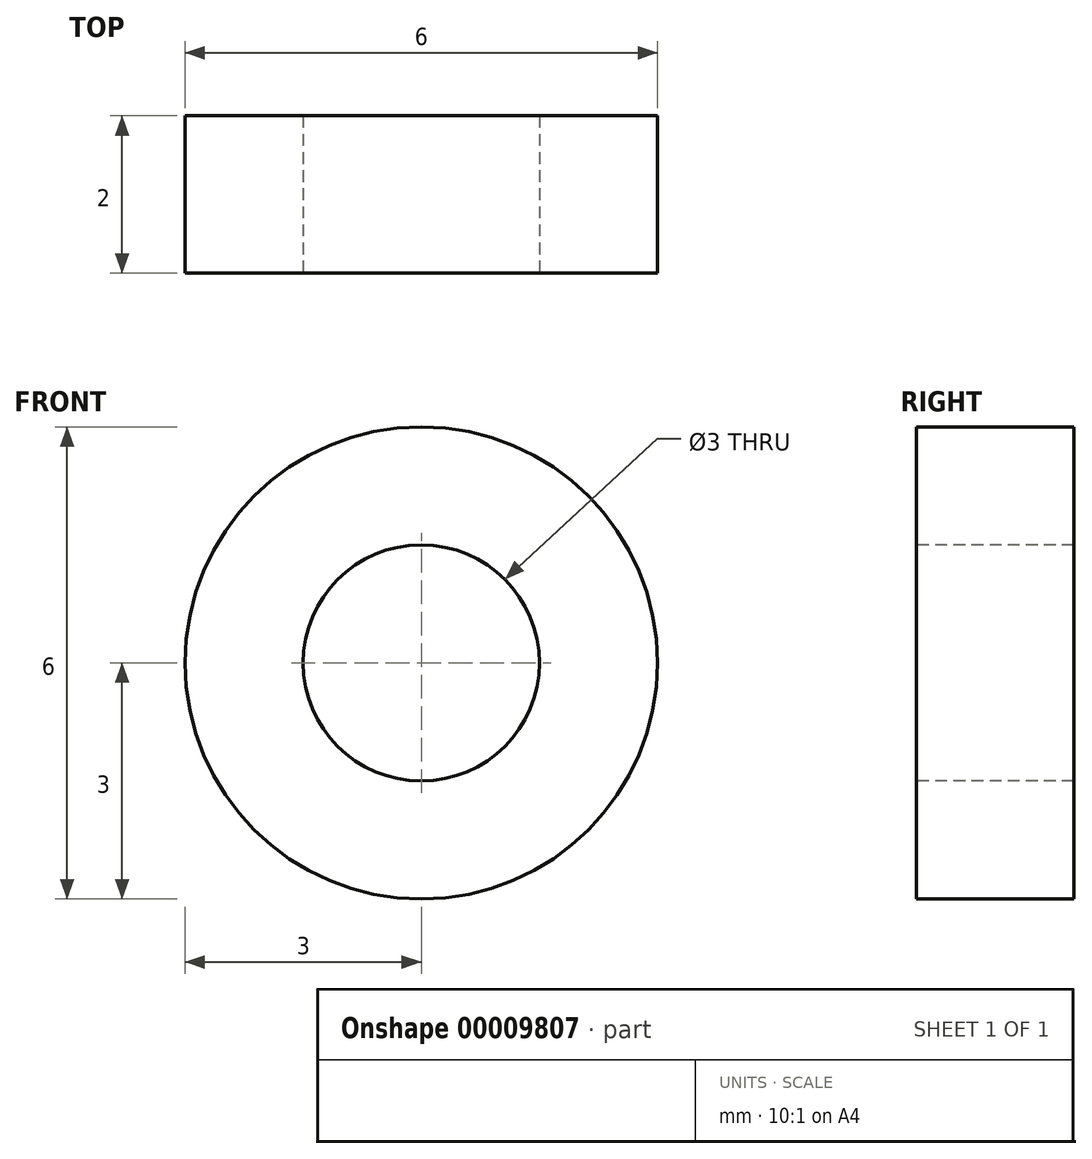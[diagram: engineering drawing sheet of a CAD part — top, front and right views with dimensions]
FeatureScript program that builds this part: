
annotation { "Feature Type Name" : "Feature", "Feature Type Description" : "" }
export const myFeature = defineFeature(function(context is Context, id is Id, definition is map)
    precondition{}
    {
        {
            var Q0;
            Q0=qCreatedBy(makeId("Front.planeOp"),FACE);
            var sketch = newSketch(context, id + "F0", { "sketchPlane" : qUnion([Q0])});
            skCircle(sketch, "E0", {"center": v(0, 0) * mm, "radius": 3 * mm});
            skSolve(sketch);
        }
        {
            var Q0;
            Q0=makeQuery(id+"F0.imprint","IMPRINT",FACE,{"disambiguationData":[TD([[makeQuery(id+"F0.imprint","IMPRINT",EDGE,{"derivedFrom":sQuery(id+"F0.wireOp",EDGE,"E0")}),1.0]])]});
            extrude(context, id + "F1", {"entities" : qUnion([Q0]), "depth" : 2 * mm});
        }
        {
            var Q0;
            Q0=makeQuery(id+"F1.opExtrude","CAP_FACE",FACE,{"disambiguationData":[OSD([sQuery(id+"F0.wireOp",EDGE,"E0")])],"isStart":false});
            var sketch = newSketch(context, id + "F2", { "sketchPlane" : qUnion([Q0])});
            skCircle(sketch, "E1", {"center": v(0, 0) * mm, "radius": 1.5 * mm});
            skSolve(sketch);
        }
        {
            var Q0;
            Q0=makeQuery(id+"F2.imprint","IMPRINT",FACE,{"disambiguationData":[TD([[makeQuery(id+"F2.imprint","IMPRINT",EDGE,{"derivedFrom":sQuery(id+"F2.wireOp",EDGE,"E1")}),1.0]])]});
            extrude(context, id + "F3", {"entities" : qUnion([Q0]), "operationType" : NewBodyOperationType.REMOVE, "oppositeDirection" : true, "depth" : 25 * mm});
        }
    });
